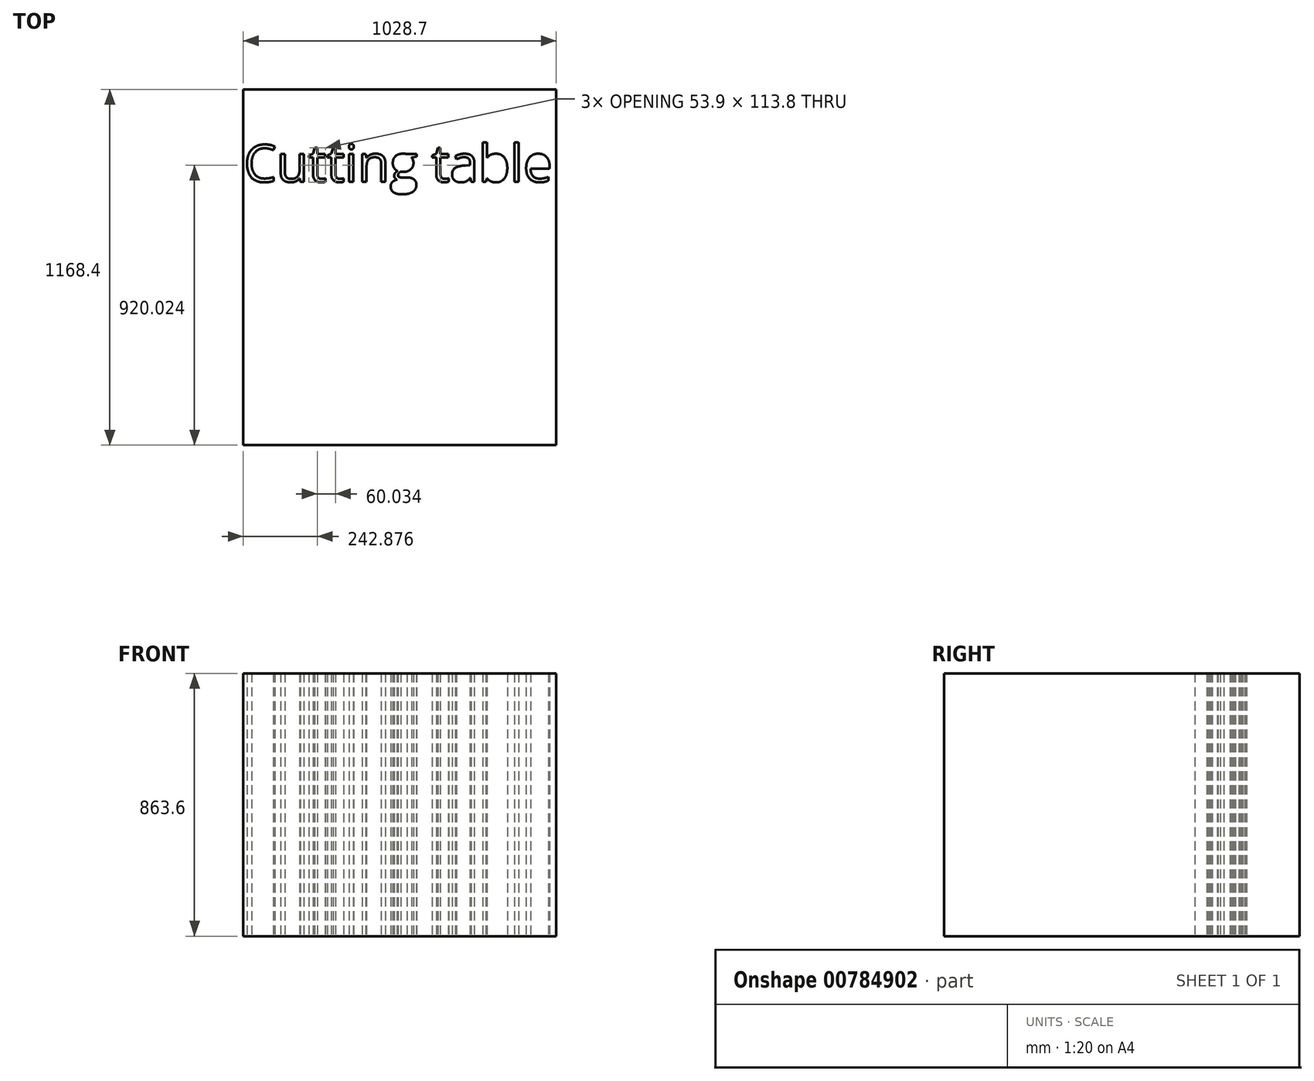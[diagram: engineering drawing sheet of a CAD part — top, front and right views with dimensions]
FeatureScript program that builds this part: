
annotation { "Feature Type Name" : "Feature", "Feature Type Description" : "" }
export const myFeature = defineFeature(function(context is Context, id is Id, definition is map)
    precondition{}
    {
        {
            var Q0;
            Q0=qCreatedBy(makeId("Top.planeOp"),FACE);
            var sketch = newSketch(context, id + "F0", { "sketchPlane" : qUnion([Q0])});
            skLineSegment(sketch, "E0.bottom", {"start": v(514.35, 584.2) * mm, "end": v(-514.35, 584.2) * mm});
            skLineSegment(sketch, "E0.top", {"start": v(514.35, -584.2) * mm, "end": v(-514.35, -584.2) * mm});
            skLineSegment(sketch, "E0.left", {"start": v(514.35, 584.2) * mm, "end": v(514.35, -584.2) * mm});
            skLineSegment(sketch, "E0.right", {"start": v(-514.35, 584.2) * mm, "end": v(-514.35, -584.2) * mm});
            skPoint(sketch, "E0.middle", {"position": v(0, 0) * mm});
            skText(sketch, "E1", { "text": "Cutting table", "fontName": "OpenSans-Regular.ttf"});
            const initialGuessF0  = {"E1": [-0.5127, 0.2806, 1, 0, 0.12246]};
            skSetInitialGuess(sketch, initialGuessF0);
            skSolve(sketch);
        }
        {
            var Q0;
            Q0=makeQuery(id+"F0.imprint","IMPRINT",FACE,{"disambiguationData":[TD([[makeQuery(id+"F0.imprint","IMPRINT",EDGE,{"derivedFrom":sQuery(id+"F0.wireOp",EDGE,"E0.bottom")}),1.0]])]});
            extrude(context, id + "F1", {"entities" : qUnion([Q0]), "depth" : 863.6 * mm, "offsetDistance" : 25.4 * mm});
        }
    });
